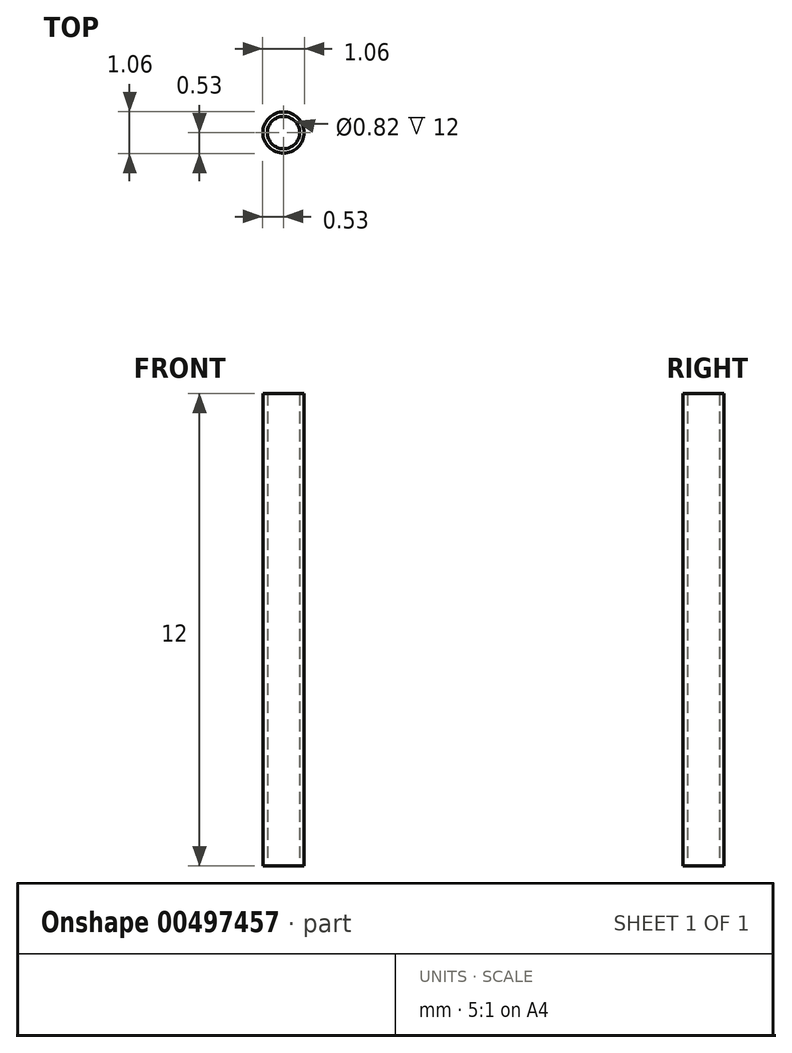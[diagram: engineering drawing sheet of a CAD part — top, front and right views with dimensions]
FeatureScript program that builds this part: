
annotation { "Feature Type Name" : "Feature", "Feature Type Description" : "" }
export const myFeature = defineFeature(function(context is Context, id is Id, definition is map)
    precondition{}
    {
        {
            var Q0;
            Q0=qCreatedBy(makeId("Top.planeOp"),FACE);
            var sketch = newSketch(context, id + "F0", { "sketchPlane" : qUnion([Q0])});
            skCircle(sketch, "E0", {"center": v(0, 0) * mm, "radius": 0.41 * mm});
            skCircle(sketch, "E1", {"center": v(0, 0) * mm, "radius": 0.53 * mm});
            skSolve(sketch);
        }
        {
            var Q0;
            Q0=makeQuery(id+"F0.imprint","IMPRINT",FACE,{"disambiguationData":[TD([[makeQuery(id+"F0.imprint","IMPRINT",EDGE,{"derivedFrom":sQuery(id+"F0.wireOp",EDGE,"E0")}),-1.0]])]});
            extrude(context, id + "F1", {"entities" : qUnion([Q0]), "depth" : 12 * mm});
        }
    });
